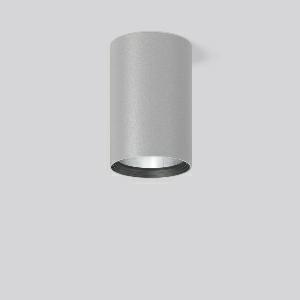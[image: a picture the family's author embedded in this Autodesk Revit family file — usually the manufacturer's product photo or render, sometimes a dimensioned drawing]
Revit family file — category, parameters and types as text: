
# Revit family: heledon_maxi_a_931245_004_2_a49b
name_source: partatom
category: Lighting Fixtures
units: mm (PartAtom-declared; Revit-internal decimal feet)

## family parameters
Cut with Voids When Loaded = No
Host = Face
Light Source = No
Part Type = Normal
Room Calculation Point = No
Round Connector Dimension = Use Diameter
Shared = No

## types (1)
- HELEDON maxi A (1 x LED Modul 927 bakery, 3400 lm, 2700)
    Apparent Load = 33 VA
    Approval mark = CE
    CIE Flux Codes = 100 100 100 100 100
    Color Rendering = 90
    Color Temperature = 2700
    Default Elevation = 1800 mm
    Description = Series: HELEDON maxi
Cylindrical surface-mounted downlight. Housing: die-cast aluminium, powder-coated. Internal ceiling frame polycarbonate with bayonet mounting. Black plastic ring and recessed LED to prevent glare from the side. Optical assembly with reflector made of MIRO-Silver with 98% total light reflection for outstanding efficiency - can be changed without tools. Special LED for illumination of pastries included. Suitable for Ceiling mounting. Easy installation with a separate ceiling frame with bayonet mounting and plug connection. Driver integrated. Connected via plug-in connector. High quality converter without flickering and stroboscopic effect. The following accessories can be mounted without use of tools: interchangeable lenses, decorative glasses, honeycomb louvre, clear and frosted diffusers, white interchangeable plastic ring. 
Colour: silver
Diameter: 123 mm
Height: 183 mm
Lamp: LED
Socket: without socket
Colour temperature: bakery
Colour rendering index (CRI): 97
System power: 33 W
Rated luminous flux: 3400 lm
Luminous efficiency: 103 lm/W
Control gear: Regulated power supply
Protection class: I
Type of protection: IP 20
    Height = 183 mm
    Lamp = 1 x LED Modul 927 bakery
    Lamp Light Flux = 3400 lm
    Lamp count = 1
    Length = 123 mm
    Lifetime = 50000 h
    Luminous efficacy = 103 lm/W
    Manufacturer = RZB
    ModVariant = No
    Model = 931245.004.2
    Mounting Place = Ceiling
    Mounting Type = Surface mounted
    Number of Poles = 1
    OnlyDefault = Yes
    Power Factor = 1
    Product Name = HELEDON maxi A
    Product group = Surface mounted downlights
    ProductGroupID = 302
    Protection Class = Protection class I
    Protection Degree = IP 20
    RLX_Detail_Level = 1
    RLX_Emergency_Light_Flux = 0 lm
    RLX_Emergency_Type = 0
    RLX_Emergency_Type_DB = No
    RlxData = <blob elided: 100353 chars, md5=1e71c09b>
    Socket = socket
    Standby Power = 0 W
    System Light Flux = 3400 lm
    System Power = 33 W
    Type Comments = Product without accessories
    Type Image = 931192.004.jpg
    URL = http://relux.com
    VarID = ---
    Voltage = 230 V
    Voltage Range = 220-240 V
    Weight = 0.00 kg
    Width = 0 mm  [stored 0 ft]

note: [stored X ft] marks values corroborated as IEEE doubles in the binary element streams (Revit-internal decimal feet)

## geometry (parser evidence)
native form markers: Blend x4, Sweep x11
no freeform markers — native parametric forms only
